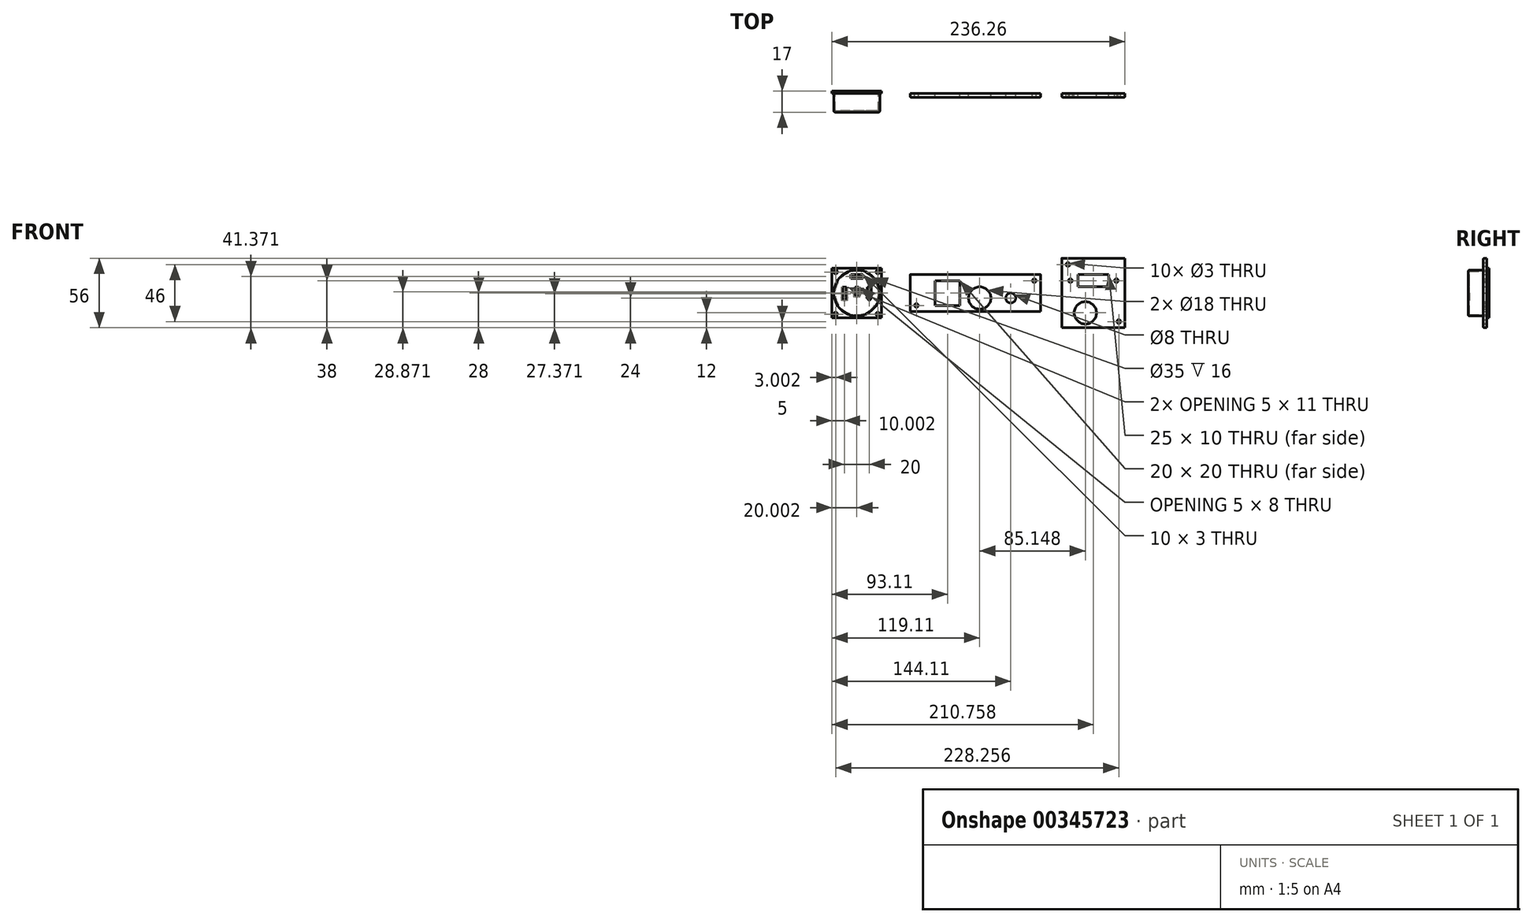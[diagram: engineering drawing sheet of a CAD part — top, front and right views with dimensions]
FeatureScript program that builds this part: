
annotation { "Feature Type Name" : "Feature", "Feature Type Description" : "" }
export const myFeature = defineFeature(function(context is Context, id is Id, definition is map)
    precondition{}
    {
        {
            var Q0;
            Q0=qCreatedBy(makeId("Front.planeOp"),FACE);
            var sketch = newSketch(context, id + "F0", { "sketchPlane" : qUnion([Q0])});
            skCircle(sketch, "E0", {"center": v(3.5, -4) * mm, "radius": 9 * mm});
            skLineSegment(sketch, "E1.bottom", {"start": v(-32.5, 10) * mm, "end": v(-12.5, 10) * mm});
            skLineSegment(sketch, "E1.top", {"start": v(-32.5, -10) * mm, "end": v(-12.5, -10) * mm});
            skLineSegment(sketch, "E1.left", {"start": v(-32.5, 10) * mm, "end": v(-32.5, -10) * mm});
            skLineSegment(sketch, "E1.right", {"start": v(-12.5, 10) * mm, "end": v(-12.5, -10) * mm});
            skCircle(sketch, "E2", {"center": v(28.5, -4) * mm, "radius": 4 * mm});
            skCircle(sketch, "E3", {"center": v(-47.5, -10) * mm, "radius": 1.5 * mm});
            skCircle(sketch, "E4", {"center": v(47.5, 10) * mm, "radius": 1.5 * mm});
            skLineSegment(sketch, "E5.bottom", {"start": v(52.5, -15) * mm, "end": v(-52.5, -15) * mm});
            skLineSegment(sketch, "E5.top", {"start": v(52.5, 15) * mm, "end": v(-52.5, 15) * mm});
            skLineSegment(sketch, "E5.left", {"start": v(52.5, -15) * mm, "end": v(52.5, 15) * mm});
            skLineSegment(sketch, "E5.right", {"start": v(-52.5, -15) * mm, "end": v(-52.5, 15) * mm});
            skPoint(sketch, "E5.middle", {"position": v(0, 0) * mm});
            skSolve(sketch);
        }
        {
            var Q0;
            Q0=makeQuery(id+"F0.imprint","IMPRINT",FACE,{"disambiguationData":[TD([[makeQuery(id+"F0.imprint","IMPRINT",EDGE,{"derivedFrom":sQuery(id+"F0.wireOp",EDGE,"E0")}),-1.0]])]});
            extrude(context, id + "F1", {"entities" : qUnion([Q0]), "depth" : 3 * mm});
        }
        {
            var Q0;
            Q0=makeQuery(id+"F1.opExtrude","CAP_EDGE",EDGE,{"disambiguationData":[OSD([sQuery(id+"F0.wireOp",EDGE,"E5.top")])],"isStart":false});
            var Q1;
            Q1=makeQuery(id+"F1.opExtrude","CAP_EDGE",EDGE,{"disambiguationData":[OSD([sQuery(id+"F0.wireOp",EDGE,"E5.right")])],"isStart":false});
            var Q2;
            Q2=makeQuery(id+"F1.opExtrude","CAP_EDGE",EDGE,{"disambiguationData":[OSD([sQuery(id+"F0.wireOp",EDGE,"E5.bottom")])],"isStart":false});
            var Q3;
            Q3=makeQuery(id+"F1.opExtrude","CAP_EDGE",EDGE,{"disambiguationData":[OSD([sQuery(id+"F0.wireOp",EDGE,"E5.left")])],"isStart":false});
            fillet(context, id + "F2", {"entities" : qUnion([Q0, Q1, Q2, Q3]), "radius" : 0.5 * mm, "tangentPropagation" : true, "allowEdgeOverflow" : false});
        }
        {
            var Q0;
            Q0=qCreatedBy(makeId("Front.planeOp"),FACE);
            var sketch = newSketch(context, id + "F3", { "sketchPlane" : qUnion([Q0])});
            skLineSegment(sketch, "E6.bottom", {"start": v(120.65, -28) * mm, "end": v(69.65, -28) * mm});
            skLineSegment(sketch, "E6.top", {"start": v(120.65, 28) * mm, "end": v(69.65, 28) * mm});
            skLineSegment(sketch, "E6.left", {"start": v(120.65, -28) * mm, "end": v(120.65, 28) * mm});
            skLineSegment(sketch, "E6.right", {"start": v(69.65, -28) * mm, "end": v(69.65, 28) * mm});
            skPoint(sketch, "E6.middle", {"position": v(95.15, 0) * mm});
            skCircle(sketch, "E7", {"center": v(74.65, 23) * mm, "radius": 1.5 * mm});
            skCircle(sketch, "E8", {"center": v(115.65, -23) * mm, "radius": 1.5 * mm});
            skCircle(sketch, "E9", {"center": v(88.65, -16) * mm, "radius": 9 * mm});
            skLineSegment(sketch, "E10.bottom", {"start": v(107.65, 5) * mm, "end": v(82.65, 5) * mm});
            skLineSegment(sketch, "E10.top", {"start": v(107.65, 15) * mm, "end": v(82.65, 15) * mm});
            skLineSegment(sketch, "E10.left", {"start": v(107.65, 5) * mm, "end": v(107.65, 15) * mm});
            skLineSegment(sketch, "E10.right", {"start": v(82.65, 5) * mm, "end": v(82.65, 15) * mm});
            skPoint(sketch, "E10.middle", {"position": v(95.15, 10) * mm});
            skCircle(sketch, "E11", {"center": v(76.65, 10) * mm, "radius": 1.5 * mm});
            skCircle(sketch, "E12", {"center": v(113.65, 10) * mm, "radius": 1.5 * mm});
            skSolve(sketch);
        }
        {
            var Q0;
            Q0=qSketchRegion(id+"F3",true);
            extrude(context, id + "F4", {"entities" : qUnion([Q0]), "depth" : 3 * mm});
        }
        {
            var Q0;
            Q0=makeQuery(id+"F4.opExtrude","CAP_EDGE",EDGE,{"disambiguationData":[OSD([sQuery(id+"F3.wireOp",EDGE,"E6.top")])],"isStart":false});
            var Q1;
            Q1=makeQuery(id+"F4.opExtrude","CAP_EDGE",EDGE,{"disambiguationData":[OSD([sQuery(id+"F3.wireOp",EDGE,"E6.right")])],"isStart":false});
            var Q2;
            Q2=makeQuery(id+"F4.opExtrude","CAP_EDGE",EDGE,{"disambiguationData":[OSD([sQuery(id+"F3.wireOp",EDGE,"E6.left")])],"isStart":false});
            var Q3;
            Q3=makeQuery(id+"F4.opExtrude","CAP_EDGE",EDGE,{"disambiguationData":[OSD([sQuery(id+"F3.wireOp",EDGE,"E6.bottom")])],"isStart":false});
            fillet(context, id + "F5", {"entities" : qUnion([Q0, Q1, Q2, Q3]), "radius" : 1 * mm, "tangentPropagation" : true, "allowEdgeOverflow" : false});
        }
        {
            var Q0;
            Q0=qCreatedBy(makeId("Front.planeOp"),FACE);
            var sketch = newSketch(context, id + "F6", { "sketchPlane" : qUnion([Q0])});
            skCircle(sketch, "E13", {"center": v(-95.6, 0) * mm, "radius": 18.5 * mm});
            skSolve(sketch);
        }
        {
            var Q0;
            Q0=qSketchRegion(id+"F6",true);
            extrude(context, id + "F7", {"entities" : qUnion([Q0]), "depth" : 15 * mm});
        }
        {
            var Q0;
            Q0=makeQuery(id+"F7.opExtrude","CAP_EDGE",EDGE,{"disambiguationData":[OSD([sQuery(id+"F6.wireOp",EDGE,"E13")])],"isStart":false});
            fillet(context, id + "F8", {"entities" : qUnion([Q0]), "radius" : 1 * mm, "tangentPropagation" : true, "allowEdgeOverflow" : false});
        }
        {
            var Q0;
            Q0=makeQuery(id+"F7.opExtrude","CAP_FACE",FACE,{"disambiguationData":[OSD([sQuery(id+"F6.wireOp",EDGE,"E13")])],"isStart":true});
            shell(context, id + "F9", {"entities" : qUnion([Q0]), "thickness" : 1 * mm});
        }
        {
            var Q0;
            Q0=makeQuery(id+"F7.opExtrude","CAP_FACE",FACE,{"disambiguationData":[OSD([sQuery(id+"F6.wireOp",EDGE,"E13"),sQuery(id+"F6.wireOp",EDGE,"Esf5itBe-Rekm-PuaR-I3QL-r79zV9LVYEKN.bottom"),sQuery(id+"F6.wireOp",EDGE,"Esf5itBe-Rekm-PuaR-I3QL-r79zV9LVYEKN.top"),sQuery(id+"F6.wireOp",EDGE,"Esf5itBe-Rekm-PuaR-I3QL-r79zV9LVYEKN.left"),sQuery(id+"F6.wireOp",EDGE,"Esf5itBe-Rekm-PuaR-I3QL-r79zV9LVYEKN.right"),sQuery(id+"F6.wireOp",EDGE,"0j1no3gY-SsaC-U71N-Fn9s-buFxBZ9oPYRc.top"),sQuery(id+"F6.wireOp",EDGE,"0j1no3gY-SsaC-U71N-Fn9s-buFxBZ9oPYRc.left"),sQuery(id+"F6.wireOp",EDGE,"0j1no3gY-SsaC-U71N-Fn9s-buFxBZ9oPYRc.right"),sQuery(id+"F6.wireOp",EDGE,"W482aUEI-9eq9-Mk7C-eVav-RZhC7vXtbm2Q"),sQuery(id+"F6.wireOp",EDGE,"a2hDfr64-Pp1r-tfV1-NXfD-V3pUvKYbAtsp"),sQuery(id+"F6.wireOp",EDGE,"u2XPa3WG-8BGT-asAA-Wqsa-QjbmhhXdVJUW"),sQuery(id+"F6.wireOp",EDGE,"EEjAVPfa-Werr-OgOK-M3jX-8QggiounJTzQ"),sQuery(id+"F6.wireOp",EDGE,"9719ca48-15b4-4f6b-9eaf-435dcdff279a.top"),sQuery(id+"F6.wireOp",EDGE,"9719ca48-15b4-4f6b-9eaf-435dcdff279a.left"),sQuery(id+"F6.wireOp",EDGE,"9719ca48-15b4-4f6b-9eaf-435dcdff279a.right"),sQuery(id+"F6.wireOp",EDGE,"ebb68154-9a52-4fc6-a236-d56a05d0ad4c"),sQuery(id+"F6.wireOp",EDGE,"eb26e9fb-7932-479b-9046-df3284eb59d3"),sQuery(id+"F6.wireOp",EDGE,"d9340d2b-f9cd-4749-837e-a9480a09c253"),sQuery(id+"F6.wireOp",EDGE,"5a250605-dac8-44e2-a521-55926b6bf676"),sQuery(id+"F6.wireOp",EDGE,"b6fd77d9-3516-4190-aba6-927b569a498c.top"),sQuery(id+"F6.wireOp",EDGE,"b6fd77d9-3516-4190-aba6-927b569a498c.left"),sQuery(id+"F6.wireOp",EDGE,"b6fd77d9-3516-4190-aba6-927b569a498c.right"),sQuery(id+"F6.wireOp",EDGE,"32018671-c3a3-447f-ad9f-cbfb8523262e"),sQuery(id+"F6.wireOp",EDGE,"b17abbf1-ba9c-4c67-9eff-51c833a29713"),sQuery(id+"F6.wireOp",EDGE,"6a737436-acba-4f85-915e-be7220d4c0c2"),sQuery(id+"F6.wireOp",EDGE,"b300f9e6-0503-4170-8434-b677de016588")])],"isStart":false});
            var sketch = newSketch(context, id + "F10", { "sketchPlane" : qUnion([Q0])});
            skLineSegment(sketch, "E14.bottom", {"start": v(-90.6, 11.87) * mm, "end": v(-100.6, 11.87) * mm});
            skLineSegment(sketch, "E14.top", {"start": v(-90.6, 14.87) * mm, "end": v(-100.6, 14.87) * mm});
            skLineSegment(sketch, "E14.left", {"start": v(-90.6, 11.87) * mm, "end": v(-90.6, 14.87) * mm});
            skLineSegment(sketch, "E14.right", {"start": v(-100.6, 11.87) * mm, "end": v(-100.6, 14.87) * mm});
            skPoint(sketch, "E14.middle", {"position": v(-95.6, 13.37) * mm});
            skLineSegment(sketch, "E15.top", {"start": v(-104.1, 4.87) * mm, "end": v(-107.1, 4.87) * mm});
            skLineSegment(sketch, "E15.left", {"start": v(-104.1, -3.13) * mm, "end": v(-104.1, 4.87) * mm});
            skLineSegment(sketch, "E15.right", {"start": v(-107.1, -3.13) * mm, "end": v(-107.1, 4.87) * mm});
            skPoint(sketch, "E15.middle", {"position": v(-105.6, 0.87) * mm});
            skLineSegment(sketch, "E16", {"start": v(-107.1, -3.13) * mm, "end": v(-108.1, -3.13) * mm});
            skLineSegment(sketch, "E17", {"start": v(-108.1, -3.13) * mm, "end": v(-105.6, -6.13) * mm});
            skLineSegment(sketch, "E18", {"start": v(-105.6, -6.13) * mm, "end": v(-103.1, -3.13) * mm});
            skLineSegment(sketch, "E19", {"start": v(-104.1, -3.13) * mm, "end": v(-103.1, -3.13) * mm});
            skLineSegment(sketch, "E20.top", {"start": v(-84.1, 4.87) * mm, "end": v(-87.1, 4.87) * mm});
            skLineSegment(sketch, "E20.left", {"start": v(-84.1, -3.13) * mm, "end": v(-84.1, 4.87) * mm});
            skLineSegment(sketch, "E20.right", {"start": v(-87.1, -3.13) * mm, "end": v(-87.1, 4.87) * mm});
            skPoint(sketch, "E20.middle", {"position": v(-85.6, 0.87) * mm});
            skLineSegment(sketch, "E21", {"start": v(-87.1, -3.13) * mm, "end": v(-88.1, -3.13) * mm});
            skLineSegment(sketch, "E22", {"start": v(-88.1, -3.13) * mm, "end": v(-85.6, -6.13) * mm});
            skLineSegment(sketch, "E23", {"start": v(-85.6, -6.13) * mm, "end": v(-83.1, -3.13) * mm});
            skLineSegment(sketch, "E24", {"start": v(-84.1, -3.13) * mm, "end": v(-83.1, -3.13) * mm});
            skLineSegment(sketch, "E25.top", {"start": v(-94.1, 4.87) * mm, "end": v(-97.1, 4.87) * mm});
            skLineSegment(sketch, "E25.left", {"start": v(-94.1, -0.13) * mm, "end": v(-94.1, 4.87) * mm});
            skLineSegment(sketch, "E25.right", {"start": v(-97.1, -0.13) * mm, "end": v(-97.1, 4.87) * mm});
            skPoint(sketch, "E25.middle", {"position": v(-95.6, 2.37) * mm});
            skLineSegment(sketch, "E26", {"start": v(-97.1, -0.13) * mm, "end": v(-98.1, -0.13) * mm});
            skLineSegment(sketch, "E27", {"start": v(-98.1, -0.13) * mm, "end": v(-95.6, -3.13) * mm});
            skLineSegment(sketch, "E28", {"start": v(-95.6, -3.13) * mm, "end": v(-93.1, -0.13) * mm});
            skLineSegment(sketch, "E29", {"start": v(-94.1, -0.13) * mm, "end": v(-93.1, -0.13) * mm});
            skSolve(sketch);
        }
        {
            var Q0;
            Q0=qSketchRegion(id+"F10",true);
            extrude(context, id + "F11", {"entities" : qUnion([Q0]), "operationType" : NewBodyOperationType.REMOVE, "oppositeDirection" : true, "depth" : 1 * mm});
        }
        {
            var Q0;
            Q0=qCreatedBy(makeId("Front.planeOp"),FACE);
            var sketch = newSketch(context, id + "F12", { "sketchPlane" : qUnion([Q0])});
            skLineSegment(sketch, "E30.bottom", {"start": v(-75.6, -20) * mm, "end": v(-115.6, -20) * mm});
            skLineSegment(sketch, "E30.top", {"start": v(-75.6, 20) * mm, "end": v(-115.6, 20) * mm});
            skLineSegment(sketch, "E30.left", {"start": v(-75.6, -20) * mm, "end": v(-75.6, 20) * mm});
            skLineSegment(sketch, "E30.right", {"start": v(-115.6, -20) * mm, "end": v(-115.6, 20) * mm});
            skPoint(sketch, "E30.middle", {"position": v(-95.6, 0) * mm});
            skCircle(sketch, "E31", {"center": v(-95.6, 0) * mm, "radius": 17.5 * mm});
            skCircle(sketch, "E32", {"center": v(-112.6, 17) * mm, "radius": 1.5 * mm});
            skCircle(sketch, "E33", {"center": v(-78.6, 17) * mm, "radius": 1.5 * mm});
            skCircle(sketch, "E34", {"center": v(-78.6, -17) * mm, "radius": 1.5 * mm});
            skCircle(sketch, "E35", {"center": v(-112.6, -17) * mm, "radius": 1.5 * mm});
            skSolve(sketch);
        }
        {
            var Q0;
            Q0=qSketchRegion(id+"F12",true);
            extrude(context, id + "F13", {"entities" : qUnion([Q0]), "operationType" : NewBodyOperationType.ADD, "oppositeDirection" : true, "depth" : 2 * mm});
        }
    });
